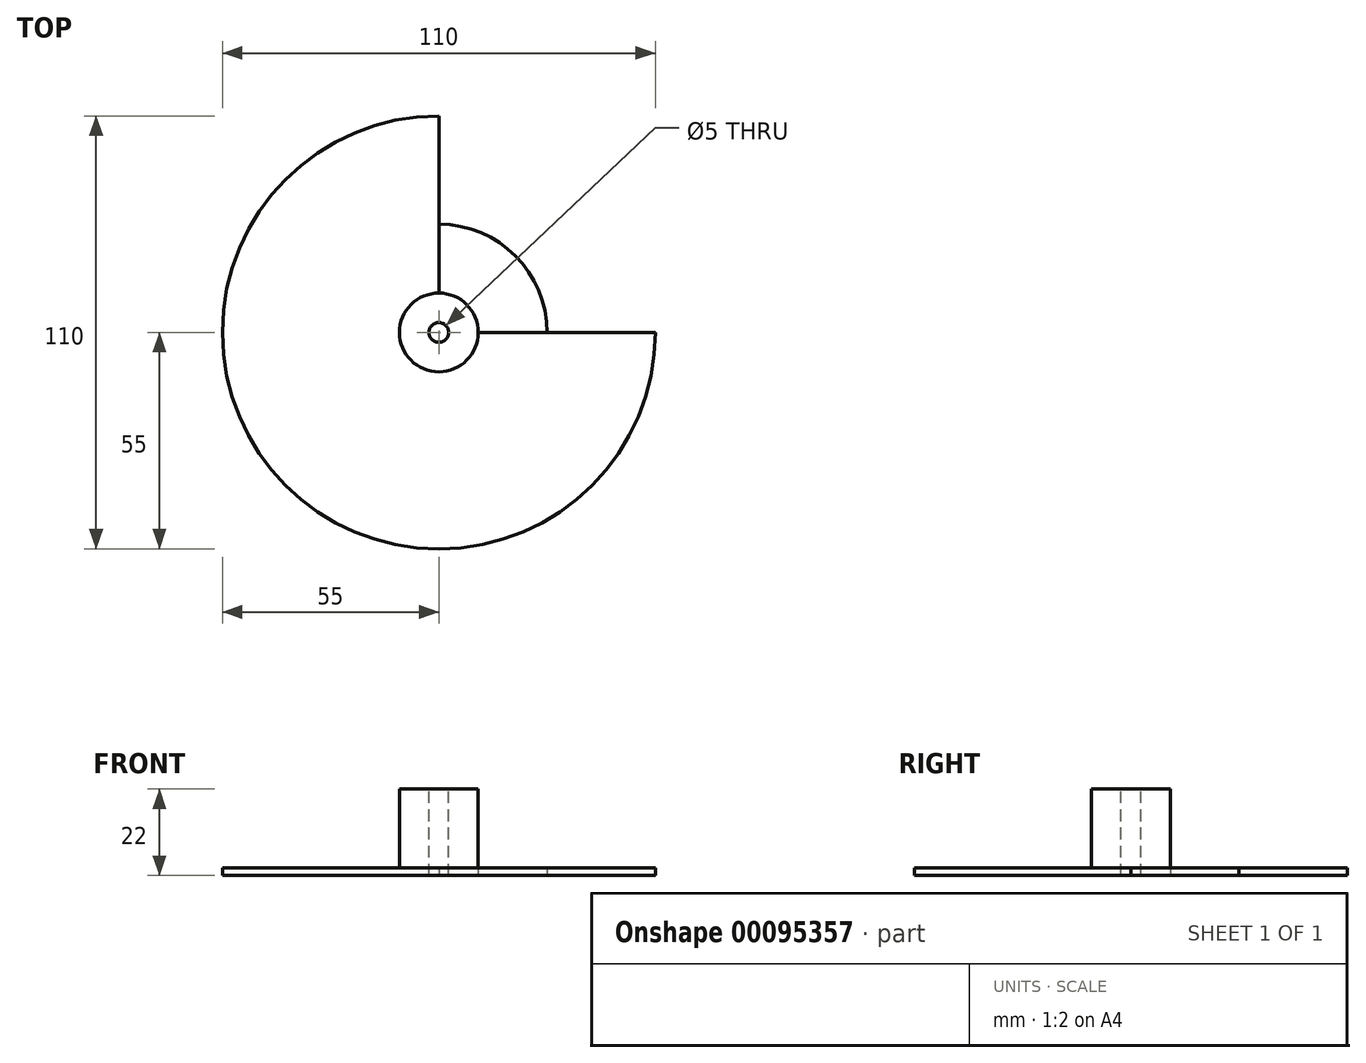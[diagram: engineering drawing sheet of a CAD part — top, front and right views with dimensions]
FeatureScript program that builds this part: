
annotation { "Feature Type Name" : "Feature", "Feature Type Description" : "" }
export const myFeature = defineFeature(function(context is Context, id is Id, definition is map)
    precondition{}
    {
        {
            var Q0;
            Q0=qCreatedBy(makeId("Top.planeOp"),FACE);
            var sketch = newSketch(context, id + "F0", { "sketchPlane" : qUnion([Q0])});
            skCircle(sketch, "E0", {"center": v(0, 0) * mm, "radius": 2.5 * mm});
            skCircle(sketch, "E1", {"center": v(0, 0) * mm, "radius": 10 * mm});
            skCircle(sketch, "E2", {"center": v(0, 0) * mm, "radius": 27.5 * mm});
            skCircle(sketch, "E3", {"center": v(0, 0) * mm, "radius": 55 * mm});
            skSolve(sketch);
        }
        {
            var Q0;
            Q0=makeQuery(id+"F0.imprint","IMPRINT",FACE,{"disambiguationData":[TD([[makeQuery(id+"F0.imprint","IMPRINT",EDGE,{"derivedFrom":sQuery(id+"F0.wireOp",EDGE,"E0")}),-1.0]])]});
            var Q1;
            Q1=makeQuery(id+"F0.imprint","IMPRINT",FACE,{"disambiguationData":[TD([[makeQuery(id+"F0.imprint","IMPRINT",EDGE,{"derivedFrom":sQuery(id+"F0.wireOp",EDGE,"E1")}),-1.0]])]});
            var Q2;
            Q2=makeQuery(id+"F0.imprint","IMPRINT",FACE,{"disambiguationData":[TD([[makeQuery(id+"F0.imprint","IMPRINT",EDGE,{"derivedFrom":sQuery(id+"F0.wireOp",EDGE,"E2")}),-1.0]])]});
            var Q3;
            Q3=sQuery(id+"F0.wireOp",EDGE,"E0");
            extrude(context, id + "F1", {"entities" : qUnion([Q0, Q1, Q2]), "surfaceEntities" : qUnion([Q3]), "oppositeDirection" : true, "depth" : 2 * mm});
        }
        {
            var Q0;
            Q0=makeQuery(id+"F1.opExtrude","CAP_FACE",FACE,{"disambiguationData":[OSD([sQuery(id+"F0.wireOp",EDGE,"E0"),sQuery(id+"F0.wireOp",EDGE,"E3")])],"isStart":true});
            var sketch = newSketch(context, id + "F2", { "sketchPlane" : qUnion([Q0])});
            skCircle(sketch, "E4", {"center": v(0, 0) * mm, "radius": 10 * mm});
            skSolve(sketch);
        }
        {
            var Q0;
            Q0=makeQuery(id+"F2.imprint","IMPRINT",FACE,{"disambiguationData":[TD([[makeQuery(id+"F2.imprint","IMPRINT",EDGE,{"derivedFrom":sQuery(id+"F2.wireOp",EDGE,"E4")}),1.0]])]});
            extrude(context, id + "F3", {"entities" : qUnion([Q0]), "operationType" : NewBodyOperationType.ADD, "depth" : 20 * mm});
        }
        {
            var Q0;
            Q0=makeQuery(id+"F1.opExtrude","CAP_FACE",FACE,{"disambiguationData":[OSD([sQuery(id+"F0.wireOp",EDGE,"E0"),sQuery(id+"F0.wireOp",EDGE,"E3")])],"isStart":false});
            var sketch = newSketch(context, id + "F4", { "sketchPlane" : qUnion([Q0])});
            skLineSegment(sketch, "E5", {"start": v(0, 0) * mm, "end": v(0, -55) * mm});
            skLineSegment(sketch, "E6", {"start": v(0, 0) * mm, "end": v(55, 0) * mm});
            skSolve(sketch);
        }
        {
            var Q0;
            {var subQ0=sQuery(id+"F4.wireOp",EDGE,"E5");var subQ1=makeQuery(id+"F1.opExtrude","CAP_EDGE",EDGE,{"disambiguationData":[OSD([sQuery(id+"F0.wireOp",EDGE,"E3")])],"isStart":false});var subQ2=makeQuery(id+"F4.imprint","INTERSECT",VERTEX,{"derivedFrom":[subQ1,subQ0]});Q0=makeQuery(id+"F4.imprint","IMPRINT",FACE,{"disambiguationData":[TD([[makeQuery(id+"F4.imprint","IMPRINT",EDGE,{"disambiguationData":[TD([[subQ2,1.0]])],"derivedFrom":subQ0}),1.0]])]});}
            extrude(context, id + "F5", {"entities" : qUnion([Q0]), "operationType" : NewBodyOperationType.REMOVE, "oppositeDirection" : true, "depth" : 2 * mm});
        }
        {
            var Q0;
            Q0=makeQuery(id+"F5.boolean.opBoolean","COPY",FACE,{"derivedFrom":makeQuery(id+"F5.opExtrude","CAP_FACE",FACE,{"disambiguationData":[OSD([sQuery(id+"F0.wireOp",EDGE,"E0"),sQuery(id+"F0.wireOp",EDGE,"E3"),sQuery(id+"F4.wireOp",EDGE,"E5"),sQuery(id+"F4.wireOp",EDGE,"E6")])],"isStart":false})});
            extrude(context, id + "F6", {"entities" : qUnion([Q0]), "operationType" : NewBodyOperationType.ADD, "depth" : 2 * mm});
        }
        {
            var Q0;
            {var subQ0=sQuery(id+"F0.wireOp",EDGE,"E3");var subQ1=sQuery(id+"F0.wireOp",EDGE,"E0");Q0=makeQuery(id+"F6.boolean.opBoolean","MERGE",FACE,{"derivedFrom":[makeQuery(id+"F1.opExtrude","CAP_FACE",FACE,{"disambiguationData":[OSD([subQ1,subQ0])],"isStart":false}),makeQuery(id+"F6.opExtrude","CAP_FACE",FACE,{"disambiguationData":[OSD([subQ1,subQ0,sQuery(id+"F4.wireOp",EDGE,"E5"),sQuery(id+"F4.wireOp",EDGE,"E6")])],"isStart":false})]});}
            var sketch = newSketch(context, id + "F7", { "sketchPlane" : qUnion([Q0])});
            skCircle(sketch, "E7", {"center": v(0, 0) * mm, "radius": 27.5 * mm});
            skSolve(sketch);
        }
        {
            var Q0;
            {var subQ5=makeQuery(id+"F6.opExtrude","CAP_EDGE",EDGE,{"disambiguationData":[OSD([sQuery(id+"F2.wireOp",EDGE,"E4")])],"isStart":false});Q0=makeQuery(id+"F7.imprint","IMPRINT",FACE,{"disambiguationData":[TD([[makeQuery(id+"F7.imprint","IMPRINT",EDGE,{"derivedFrom":subQ5}),1.0]])]});}
            extrude(context, id + "F8", {"entities" : qUnion([Q0]), "depth" : 2 * mm});
        }
        {
            var Q0;
            Q0=makeQuery(id+"F8.opExtrude","CAP_FACE",FACE,{"disambiguationData":[OSD([sQuery(id+"F2.wireOp",EDGE,"E4"),sQuery(id+"F4.wireOp",EDGE,"E5"),sQuery(id+"F4.wireOp",EDGE,"E6"),sQuery(id+"F7.wireOp",EDGE,"E7")])],"isStart":true});
            extrude(context, id + "F9", {"entities" : qUnion([Q0]), "depth" : 2 * mm});
        }
        {
            var Q0;
            Q0=makeQuery(id+"F8.opExtrude","CAP_FACE",FACE,{"disambiguationData":[OSD([sQuery(id+"F2.wireOp",EDGE,"E4"),sQuery(id+"F4.wireOp",EDGE,"E5"),sQuery(id+"F4.wireOp",EDGE,"E6"),sQuery(id+"F7.wireOp",EDGE,"E7")])],"isStart":false});
            extrude(context, id + "F10", {"entities" : qUnion([Q0]), "operationType" : NewBodyOperationType.REMOVE, "oppositeDirection" : true, "depth" : 2 * mm});
        }
    });
